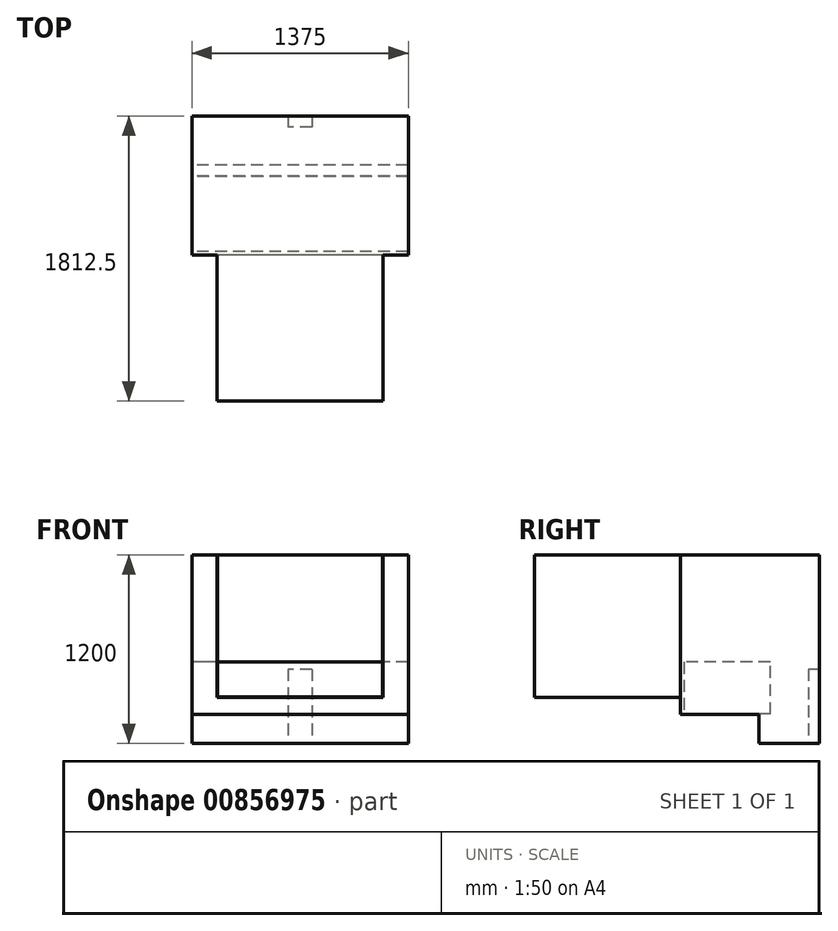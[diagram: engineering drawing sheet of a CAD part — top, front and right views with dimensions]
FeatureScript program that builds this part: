
annotation { "Feature Type Name" : "Feature", "Feature Type Description" : "" }
export const myFeature = defineFeature(function(context is Context, id is Id, definition is map)
    precondition{}
    {
        {
            var Q0;
            Q0=qCreatedBy(makeId("Right.planeOp"),FACE);
            var sketch = newSketch(context, id + "F0", { "sketchPlane" : qUnion([Q0])});
            skLineSegment(sketch, "E0", {"start": v(0, 0) * mm, "end": v(0, -725) * mm});
            skLineSegment(sketch, "E1", {"start": v(-70, -1195) * mm, "end": v(-380, -1195) * mm});
            skLineSegment(sketch, "E2", {"start": v(-380, -1195) * mm, "end": v(-380, -1010) * mm});
            skLineSegment(sketch, "E3", {"start": v(-380, -1010) * mm, "end": v(-880, -1010) * mm});
            skLineSegment(sketch, "E4", {"start": v(-880, -1010) * mm, "end": v(-880, -900) * mm});
            skLineSegment(sketch, "E5", {"start": v(-880, -900) * mm, "end": v(-1810, -900) * mm});
            skLineSegment(sketch, "E6", {"start": v(-1810, -900) * mm, "end": v(-1810, 0) * mm});
            skLineSegment(sketch, "E7", {"start": v(-1810, 0) * mm, "end": v(0, 0) * mm});
            skLineSegment(sketch, "E8", {"start": v(-880, -900) * mm, "end": v(-880, 0) * mm});
            skLineSegment(sketch, "E9", {"start": v(-380, -1010) * mm, "end": v(-310, -1010) * mm});
            skLineSegment(sketch, "E10", {"start": v(-310, -1010) * mm, "end": v(-310, -678.42) * mm});
            skLineSegment(sketch, "E11", {"start": v(-310, -678.42) * mm, "end": v(-860, -678.42) * mm});
            skLineSegment(sketch, "E12", {"start": v(-860, -678.42) * mm, "end": v(-860, -1010) * mm});
            skLineSegment(sketch, "E13", {"start": v(0, -725) * mm, "end": v(0, -1195) * mm});
            skLineSegment(sketch, "E14", {"start": v(0, -1195) * mm, "end": v(-70, -1195) * mm});
            skLineSegment(sketch, "E15", {"start": v(0, -725) * mm, "end": v(-70, -725) * mm});
            skLineSegment(sketch, "E16", {"start": v(-70, -725) * mm, "end": v(-70, -1195) * mm});
            skSolve(sketch);
        }
        {
            var Q0;
            {var subQ2=sQuery(id+"F0.wireOp",EDGE,"E0");Q0=makeQuery(id+"F0.imprint","IMPRINT",FACE,{"disambiguationData":[TD([[makeQuery(id+"F0.imprint","IMPRINT",EDGE,{"derivedFrom":subQ2}),-1.0]])]});}
            var Q1;
            Q1=makeQuery(id+"F0.imprint","IMPRINT",FACE,{"disambiguationData":[TD([[makeQuery(id+"F0.imprint","IMPRINT",EDGE,{"derivedFrom":sQuery(id+"F0.wireOp",EDGE,"E13")}),-1.0]])]});
            var Q2;
            {var subQ0=sQuery(id+"F0.wireOp",EDGE,"E9");Q2=makeQuery(id+"F0.imprint","IMPRINT",FACE,{"disambiguationData":[TD([[makeQuery(id+"F0.imprint","IMPRINT",EDGE,{"derivedFrom":subQ0}),1.0]])]});}
            extrude(context, id + "F1", {"entities" : qUnion([Q0, Q1, Q2]), "depth" : 1370 * mm, "offsetDistance" : 25 * mm, "symmetric" : true});
        }
        {
            var Q0;
            Q0=makeQuery(id+"F0.imprint","IMPRINT",FACE,{"disambiguationData":[TD([[makeQuery(id+"F0.imprint","IMPRINT",EDGE,{"derivedFrom":sQuery(id+"F0.wireOp",EDGE,"E5")}),-1.0]])]});
            extrude(context, id + "F2", {"entities" : qUnion([Q0]), "operationType" : NewBodyOperationType.ADD, "depth" : 1050 * mm, "offsetDistance" : 25 * mm, "symmetric" : true});
        }
        {
            var Q0;
            Q0=makeQuery(id+"F2.opExtrude","SWEPT_FACE",FACE,{"disambiguationData":[OSD([sQuery(id+"F0.wireOp",EDGE,"E6")])]});
            shell(context, id + "F3", {"entities" : qUnion([Q0]), "thickness" : 2.5 * mm, "oppositeDirection" : true});
        }
        {
            var Q0;
            {var subQ0=sQuery(id+"F0.wireOp",EDGE,"E9");Q0=makeQuery(id+"F0.imprint","IMPRINT",FACE,{"disambiguationData":[TD([[makeQuery(id+"F0.imprint","IMPRINT",EDGE,{"derivedFrom":subQ0}),1.0]])]});}
            extrude(context, id + "F4", {"entities" : qUnion([Q0]), "operationType" : NewBodyOperationType.ADD, "depth" : 1370 * mm, "offsetDistance" : 25 * mm, "symmetric" : true});
        }
        {
            var Q0;
            Q0=makeQuery(id+"F0.imprint","IMPRINT",FACE,{"disambiguationData":[TD([[makeQuery(id+"F0.imprint","IMPRINT",EDGE,{"derivedFrom":sQuery(id+"F0.wireOp",EDGE,"E13")}),-1.0]])]});
            extrude(context, id + "F5", {"entities" : qUnion([Q0]), "operationType" : NewBodyOperationType.ADD, "depth" : 150 * mm, "offsetDistance" : 25 * mm, "symmetric" : true});
        }
        {
            var Q0;
            Q0=makeQuery(id+"F3.opShell","OFFSET_FACE",FACE,{"disambiguationData":[OSD([sQuery(id+"F0.wireOp",EDGE,"E5")])]});
            var sketch = newSketch(context, id + "F6", { "sketchPlane" : qUnion([Q0])});
            skLineSegment(sketch, "E17", {"start": v(-525, -1810) * mm, "end": v(-515, -1810) * mm, "construction": true});
            skLineSegment(sketch, "E18", {"start": v(-515, -1810) * mm, "end": v(-515, -1800) * mm, "construction": true});
            skSolve(sketch);
        }
    });
